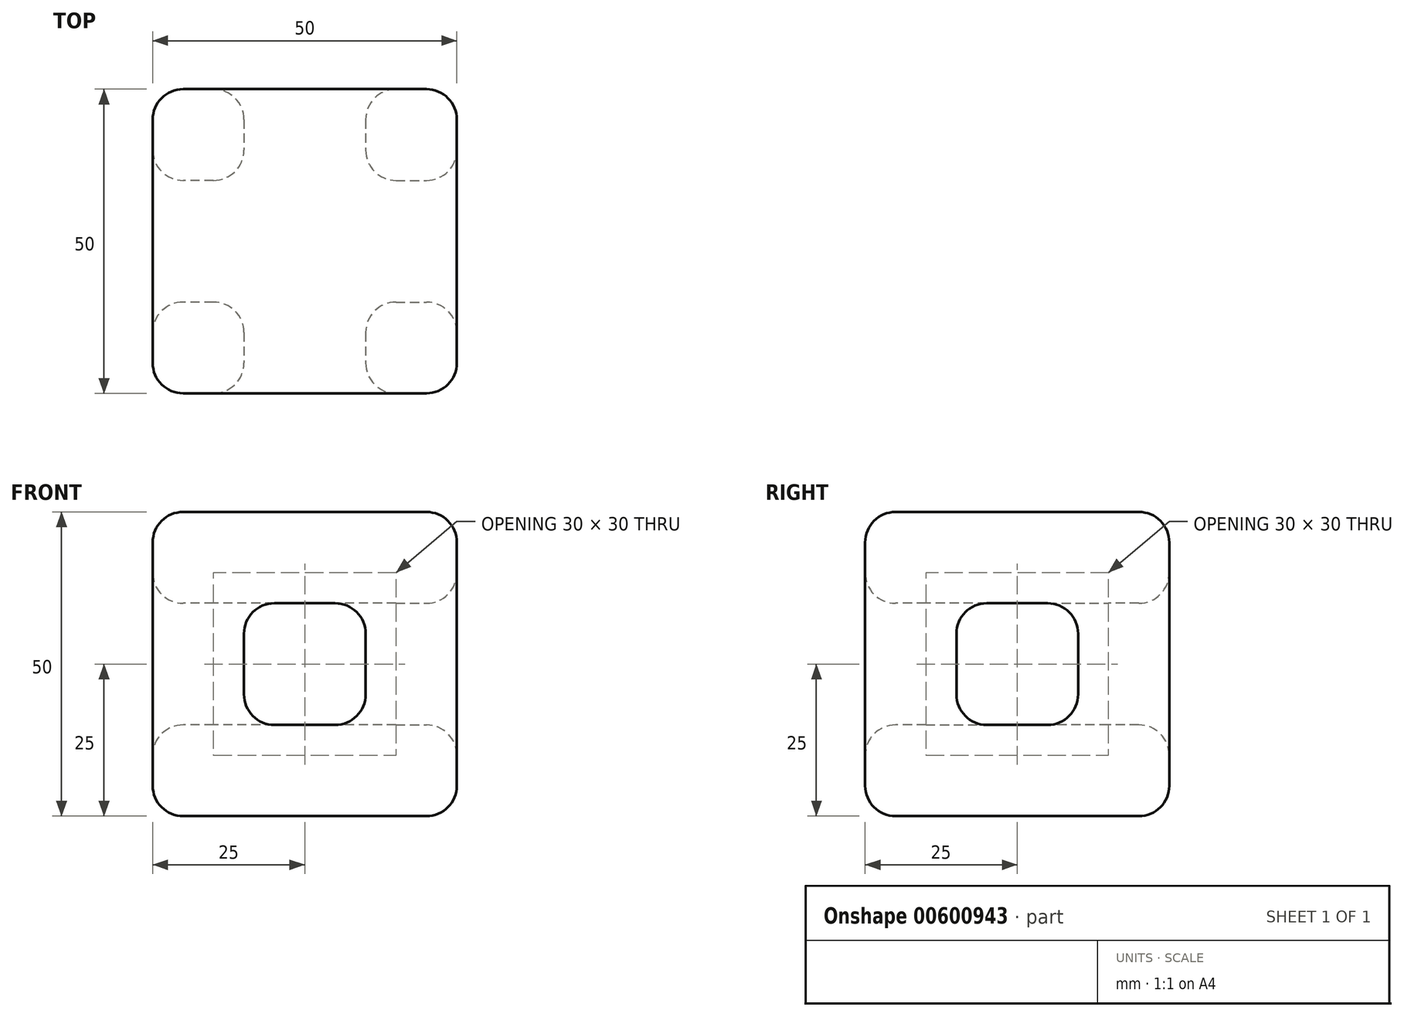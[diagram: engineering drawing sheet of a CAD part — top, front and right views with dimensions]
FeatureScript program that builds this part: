
annotation { "Feature Type Name" : "Feature", "Feature Type Description" : "" }
export const myFeature = defineFeature(function(context is Context, id is Id, definition is map)
    precondition{}
    {
        {
            var Q0;
            Q0=qCreatedBy(makeId("Front.planeOp"),FACE);
            var sketch = newSketch(context, id + "F0", { "sketchPlane" : qUnion([Q0])});
            skLineSegment(sketch, "E0.bottom", {"start": v(25, -25) * mm, "end": v(-25, -25) * mm});
            skLineSegment(sketch, "E0.top", {"start": v(25, 25) * mm, "end": v(-25, 25) * mm});
            skLineSegment(sketch, "E0.left", {"start": v(25, -25) * mm, "end": v(25, 25) * mm});
            skLineSegment(sketch, "E0.right", {"start": v(-25, -25) * mm, "end": v(-25, 25) * mm});
            skPoint(sketch, "E0.middle", {"position": v(0, 0) * mm});
            skSolve(sketch);
        }
        {
            var Q0;
            Q0 = qSketchRegion(id + "F0", true);
            extrude(context, id + "F1", {"entities" : qUnion([Q0]), "depth" : 25 * mm, "offsetDistance" : 25 * mm, "hasSecondDirection" : true, "secondDirectionOppositeDirection" : true, "secondDirectionDepth" : 25 * mm});
        }
        {
            var Q0;
            Q0=makeQuery(id+"F1.opExtrude","CAP_FACE",FACE,{"disambiguationData":[OSD([sQuery(id+"F0.wireOp",EDGE,"E0.bottom"),sQuery(id+"F0.wireOp",EDGE,"E0.top"),sQuery(id+"F0.wireOp",EDGE,"E0.left"),sQuery(id+"F0.wireOp",EDGE,"E0.right")])],"isStart":false});
            var sketch = newSketch(context, id + "F2", { "sketchPlane" : qUnion([Q0])});
            skLineSegment(sketch, "E1.bottom", {"start": v(10, 10) * mm, "end": v(-10, 10) * mm});
            skLineSegment(sketch, "E1.top", {"start": v(10, -10) * mm, "end": v(-10, -10) * mm});
            skLineSegment(sketch, "E1.left", {"start": v(10, 10) * mm, "end": v(10, -10) * mm});
            skLineSegment(sketch, "E1.right", {"start": v(-10, 10) * mm, "end": v(-10, -10) * mm});
            skPoint(sketch, "E1.middle", {"position": v(0, 0) * mm});
            skSolve(sketch);
        }
        {
            var Q0;
            Q0=makeQuery(id+"F2.imprint","IMPRINT",FACE,{"disambiguationData":[TD([[makeQuery(id+"F2.imprint","IMPRINT",EDGE,{"derivedFrom":sQuery(id+"F2.wireOp",EDGE,"E1.bottom")}),1.0]])]});
            extrude(context, id + "F3", {"entities" : qUnion([Q0]), "operationType" : NewBodyOperationType.REMOVE, "endBound" : BoundingType.UP_TO_NEXT, "oppositeDirection" : true, "depth" : 25 * mm, "offsetDistance" : 25 * mm});
        }
        {
            var Q0;
            Q0=makeQuery(id+"F1.opExtrude","SWEPT_FACE",FACE,{"disambiguationData":[OSD([sQuery(id+"F0.wireOp",EDGE,"E0.right")])]});
            var sketch = newSketch(context, id + "F4", { "sketchPlane" : qUnion([Q0])});
            skLineSegment(sketch, "E2.bottom", {"start": v(-10, 10) * mm, "end": v(10, 10) * mm});
            skLineSegment(sketch, "E2.top", {"start": v(-10, -10) * mm, "end": v(10, -10) * mm});
            skLineSegment(sketch, "E2.left", {"start": v(-10, 10) * mm, "end": v(-10, -10) * mm});
            skLineSegment(sketch, "E2.right", {"start": v(10, 10) * mm, "end": v(10, -10) * mm});
            skPoint(sketch, "E2.middle", {"position": v(0, 0) * mm});
            skSolve(sketch);
        }
        {
            var Q0;
            Q0=makeQuery(id+"F4.imprint","IMPRINT",FACE,{"disambiguationData":[TD([[makeQuery(id+"F4.imprint","IMPRINT",EDGE,{"derivedFrom":sQuery(id+"F4.wireOp",EDGE,"E2.bottom")}),-1.0]])]});
            extrude(context, id + "F5", {"entities" : qUnion([Q0]), "operationType" : NewBodyOperationType.REMOVE, "endBound" : BoundingType.UP_TO_NEXT, "oppositeDirection" : true, "depth" : 25 * mm, "offsetDistance" : 25 * mm});
        }
        {
            var Q0;
            Q0=makeQuery(id+"F1.opExtrude","SWEPT_FACE",FACE,{"disambiguationData":[OSD([sQuery(id+"F0.wireOp",EDGE,"E0.left")])]});
            var sketch = newSketch(context, id + "F6", { "sketchPlane" : qUnion([Q0])});
            skLineSegment(sketch, "E3.bottom", {"start": v(-10, 10) * mm, "end": v(10, 10) * mm});
            skLineSegment(sketch, "E3.top", {"start": v(-10, -10) * mm, "end": v(10, -10) * mm});
            skLineSegment(sketch, "E3.left", {"start": v(-10, 10) * mm, "end": v(-10, -10) * mm});
            skLineSegment(sketch, "E3.right", {"start": v(10, 10) * mm, "end": v(10, -10) * mm});
            skPoint(sketch, "E3.middle", {"position": v(0, 0) * mm});
            skSolve(sketch);
        }
        {
            var Q0;
            Q0=makeQuery(id+"F6.imprint","IMPRINT",FACE,{"disambiguationData":[TD([[makeQuery(id+"F6.imprint","IMPRINT",EDGE,{"derivedFrom":sQuery(id+"F6.wireOp",EDGE,"E3.bottom")}),-1.0]])]});
            extrude(context, id + "F7", {"entities" : qUnion([Q0]), "operationType" : NewBodyOperationType.REMOVE, "endBound" : BoundingType.UP_TO_NEXT, "oppositeDirection" : true, "depth" : 25 * mm, "offsetDistance" : 25 * mm});
        }
        {
            var Q0;
            Q0=makeQuery(id+"F1.opExtrude","SWEPT_EDGE",EDGE,{"disambiguationData":[OSD([sQuery(id+"F0.wireOp",EDGE,"E0.top"),sQuery(id+"F0.wireOp",EDGE,"E0.right")])]});
            var Q1;
            Q1=makeQuery(id+"F1.opExtrude","SWEPT_EDGE",EDGE,{"disambiguationData":[OSD([sQuery(id+"F0.wireOp",EDGE,"E0.top"),sQuery(id+"F0.wireOp",EDGE,"E0.left")])]});
            var Q2;
            Q2=makeQuery(id+"F3.boolean.opBoolean","COPY",EDGE,{"derivedFrom":makeQuery(id+"F3.opExtrude","TWEAK_EDGE",EDGE,{"derivedFrom":[makeQuery(id+"F1.opExtrude","CAP_FACE",FACE,{"disambiguationData":[OSD([sQuery(id+"F0.wireOp",EDGE,"E0.bottom"),sQuery(id+"F0.wireOp",EDGE,"E0.top"),sQuery(id+"F0.wireOp",EDGE,"E0.left"),sQuery(id+"F0.wireOp",EDGE,"E0.right")])],"isStart":true}),makeQuery(id+"F2.imprint","IMPRINT",EDGE,{"derivedFrom":sQuery(id+"F2.wireOp",EDGE,"E1.bottom")})]})});
            var Q3;
            Q3=makeQuery(id+"F1.opExtrude","SWEPT_EDGE",EDGE,{"disambiguationData":[OSD([sQuery(id+"F0.wireOp",EDGE,"E0.bottom"),sQuery(id+"F0.wireOp",EDGE,"E0.right")])]});
            var Q4;
            Q4=makeQuery(id+"F1.opExtrude","SWEPT_EDGE",EDGE,{"disambiguationData":[OSD([sQuery(id+"F0.wireOp",EDGE,"E0.bottom"),sQuery(id+"F0.wireOp",EDGE,"E0.left")])]});
            var Q5;
            Q5=makeQuery(id+"F1.opExtrude","CAP_EDGE",EDGE,{"disambiguationData":[OSD([sQuery(id+"F0.wireOp",EDGE,"E0.top")])],"isStart":false});
            var Q6;
            Q6=makeQuery(id+"F1.opExtrude","CAP_EDGE",EDGE,{"disambiguationData":[OSD([sQuery(id+"F0.wireOp",EDGE,"E0.bottom")])],"isStart":false});
            var Q7;
            Q7=makeQuery(id+"F1.opExtrude","CAP_EDGE",EDGE,{"disambiguationData":[OSD([sQuery(id+"F0.wireOp",EDGE,"E0.top")])],"isStart":true});
            var Q8;
            Q8=makeQuery(id+"F1.opExtrude","CAP_EDGE",EDGE,{"disambiguationData":[OSD([sQuery(id+"F0.wireOp",EDGE,"E0.bottom")])],"isStart":true});
            var Q9;
            Q9=makeQuery(id+"F1.opExtrude","CAP_EDGE",EDGE,{"disambiguationData":[OSD([sQuery(id+"F0.wireOp",EDGE,"E0.left")])],"isStart":true});
            var Q10;
            Q10=makeQuery(id+"F1.opExtrude","CAP_EDGE",EDGE,{"disambiguationData":[OSD([sQuery(id+"F0.wireOp",EDGE,"E0.left")])],"isStart":false});
            var Q11;
            Q11=makeQuery(id+"F1.opExtrude","CAP_EDGE",EDGE,{"disambiguationData":[OSD([sQuery(id+"F0.wireOp",EDGE,"E0.right")])],"isStart":true});
            var Q12;
            Q12=makeQuery(id+"F1.opExtrude","CAP_EDGE",EDGE,{"disambiguationData":[OSD([sQuery(id+"F0.wireOp",EDGE,"E0.right")])],"isStart":false});
            var Q13;
            Q13=makeQuery(id+"F3.boolean.opBoolean","COPY",EDGE,{"derivedFrom":makeQuery(id+"F3.opExtrude","TWEAK_EDGE",EDGE,{"derivedFrom":[makeQuery(id+"F1.opExtrude","CAP_FACE",FACE,{"disambiguationData":[OSD([sQuery(id+"F0.wireOp",EDGE,"E0.bottom"),sQuery(id+"F0.wireOp",EDGE,"E0.top"),sQuery(id+"F0.wireOp",EDGE,"E0.left"),sQuery(id+"F0.wireOp",EDGE,"E0.right")])],"isStart":true}),makeQuery(id+"F2.imprint","IMPRINT",EDGE,{"derivedFrom":sQuery(id+"F2.wireOp",EDGE,"E1.top")})]})});
            var Q14;
            Q14=makeQuery(id+"F3.boolean.opBoolean","COPY",EDGE,{"derivedFrom":makeQuery(id+"F3.opExtrude","TWEAK_EDGE",EDGE,{"derivedFrom":[makeQuery(id+"F1.opExtrude","CAP_FACE",FACE,{"disambiguationData":[OSD([sQuery(id+"F0.wireOp",EDGE,"E0.bottom"),sQuery(id+"F0.wireOp",EDGE,"E0.top"),sQuery(id+"F0.wireOp",EDGE,"E0.left"),sQuery(id+"F0.wireOp",EDGE,"E0.right")])],"isStart":true}),makeQuery(id+"F2.imprint","IMPRINT",EDGE,{"derivedFrom":sQuery(id+"F2.wireOp",EDGE,"E1.left")})]})});
            var Q15;
            Q15=makeQuery(id+"F3.boolean.opBoolean","COPY",EDGE,{"derivedFrom":makeQuery(id+"F3.opExtrude","TWEAK_EDGE",EDGE,{"derivedFrom":[makeQuery(id+"F1.opExtrude","CAP_FACE",FACE,{"disambiguationData":[OSD([sQuery(id+"F0.wireOp",EDGE,"E0.bottom"),sQuery(id+"F0.wireOp",EDGE,"E0.top"),sQuery(id+"F0.wireOp",EDGE,"E0.left"),sQuery(id+"F0.wireOp",EDGE,"E0.right")])],"isStart":true}),makeQuery(id+"F2.imprint","IMPRINT",EDGE,{"derivedFrom":sQuery(id+"F2.wireOp",EDGE,"E1.right")})]})});
            var Q16;
            Q16=makeQuery(id+"F7.boolean.opBoolean","COPY",EDGE,{"derivedFrom":makeQuery(id+"F7.opExtrude","TWEAK_EDGE",EDGE,{"derivedFrom":[makeQuery(id+"F3.boolean.opBoolean","COPY",FACE,{"derivedFrom":makeQuery(id+"F3.opExtrude","SWEPT_FACE",FACE,{"disambiguationData":[OSD([sQuery(id+"F2.wireOp",EDGE,"E1.left")])]})}),makeQuery(id+"F6.imprint","IMPRINT",EDGE,{"derivedFrom":sQuery(id+"F6.wireOp",EDGE,"E3.left")})]})});
            var Q17;
            Q17=makeQuery(id+"F1.opExtrude","CAP_FACE",FACE,{"disambiguationData":[OSD([sQuery(id+"F0.wireOp",EDGE,"E0.bottom"),sQuery(id+"F0.wireOp",EDGE,"E0.top"),sQuery(id+"F0.wireOp",EDGE,"E0.left"),sQuery(id+"F0.wireOp",EDGE,"E0.right")])],"isStart":true});
            var Q18;
            Q18=makeQuery(id+"F5.boolean.opBoolean","COPY",EDGE,{"derivedFrom":makeQuery(id+"F5.opExtrude","SWEPT_EDGE",EDGE,{"disambiguationData":[OSD([sQuery(id+"F4.wireOp",EDGE,"E2.bottom"),sQuery(id+"F4.wireOp",EDGE,"E2.left")])]})});
            var Q19;
            Q19=makeQuery(id+"F3.boolean.opBoolean","COPY",EDGE,{"derivedFrom":makeQuery(id+"F3.opExtrude","CAP_EDGE",EDGE,{"disambiguationData":[OSD([sQuery(id+"F2.wireOp",EDGE,"E1.bottom")])],"isStart":true})});
            var Q20;
            Q20=makeQuery(id+"F3.boolean.opBoolean","COPY",EDGE,{"derivedFrom":makeQuery(id+"F3.opExtrude","CAP_EDGE",EDGE,{"disambiguationData":[OSD([sQuery(id+"F2.wireOp",EDGE,"E1.top")])],"isStart":true})});
            var Q21;
            Q21=makeQuery(id+"F3.boolean.opBoolean","COPY",EDGE,{"derivedFrom":makeQuery(id+"F3.opExtrude","CAP_EDGE",EDGE,{"disambiguationData":[OSD([sQuery(id+"F2.wireOp",EDGE,"E1.right")])],"isStart":true})});
            var Q22;
            Q22=makeQuery(id+"F5.boolean.opBoolean","COPY",EDGE,{"derivedFrom":makeQuery(id+"F5.opExtrude","CAP_EDGE",EDGE,{"disambiguationData":[OSD([sQuery(id+"F4.wireOp",EDGE,"E2.left")])],"isStart":true})});
            var Q23;
            Q23=makeQuery(id+"F5.boolean.opBoolean","COPY",EDGE,{"derivedFrom":makeQuery(id+"F5.opExtrude","SWEPT_EDGE",EDGE,{"disambiguationData":[OSD([sQuery(id+"F4.wireOp",EDGE,"E2.top"),sQuery(id+"F4.wireOp",EDGE,"E2.right")])]})});
            var Q24;
            Q24=makeQuery(id+"F5.boolean.opBoolean","COPY",EDGE,{"derivedFrom":makeQuery(id+"F5.opExtrude","SWEPT_EDGE",EDGE,{"disambiguationData":[OSD([sQuery(id+"F4.wireOp",EDGE,"E2.top"),sQuery(id+"F4.wireOp",EDGE,"E2.left")])]})});
            var Q25;
            Q25=makeQuery(id+"F7.boolean.opBoolean","COPY",EDGE,{"derivedFrom":makeQuery(id+"F7.opExtrude","TWEAK_EDGE",EDGE,{"derivedFrom":[makeQuery(id+"F3.boolean.opBoolean","COPY",FACE,{"derivedFrom":makeQuery(id+"F3.opExtrude","SWEPT_FACE",FACE,{"disambiguationData":[OSD([sQuery(id+"F2.wireOp",EDGE,"E1.left")])]})}),makeQuery(id+"F6.imprint","IMPRINT",EDGE,{"derivedFrom":sQuery(id+"F6.wireOp",EDGE,"E3.right")})]})});
            var Q26;
            Q26=makeQuery(id+"F7.boolean.opBoolean","COPY",EDGE,{"derivedFrom":makeQuery(id+"F7.opExtrude","SWEPT_EDGE",EDGE,{"disambiguationData":[OSD([sQuery(id+"F6.wireOp",EDGE,"E3.bottom"),sQuery(id+"F6.wireOp",EDGE,"E3.left")])]})});
            var Q27;
            Q27=makeQuery(id+"F7.boolean.opBoolean","COPY",EDGE,{"derivedFrom":makeQuery(id+"F7.opExtrude","SWEPT_EDGE",EDGE,{"disambiguationData":[OSD([sQuery(id+"F6.wireOp",EDGE,"E3.bottom"),sQuery(id+"F6.wireOp",EDGE,"E3.right")])]})});
            var Q28;
            Q28=makeQuery(id+"F7.boolean.opBoolean","COPY",EDGE,{"derivedFrom":makeQuery(id+"F7.opExtrude","SWEPT_EDGE",EDGE,{"disambiguationData":[OSD([sQuery(id+"F6.wireOp",EDGE,"E3.top"),sQuery(id+"F6.wireOp",EDGE,"E3.left")])]})});
            var Q29;
            Q29=makeQuery(id+"F7.boolean.opBoolean","COPY",EDGE,{"derivedFrom":makeQuery(id+"F7.opExtrude","SWEPT_EDGE",EDGE,{"disambiguationData":[OSD([sQuery(id+"F6.wireOp",EDGE,"E3.top"),sQuery(id+"F6.wireOp",EDGE,"E3.right")])]})});
            var Q30;
            Q30=makeQuery(id+"F7.boolean.opBoolean","COPY",EDGE,{"derivedFrom":makeQuery(id+"F7.opExtrude","CAP_EDGE",EDGE,{"disambiguationData":[OSD([sQuery(id+"F6.wireOp",EDGE,"E3.left")])],"isStart":true})});
            var Q31;
            Q31=makeQuery(id+"F7.boolean.opBoolean","COPY",EDGE,{"derivedFrom":makeQuery(id+"F7.opExtrude","CAP_EDGE",EDGE,{"disambiguationData":[OSD([sQuery(id+"F6.wireOp",EDGE,"E3.right")])],"isStart":true})});
            var Q32;
            Q32=makeQuery(id+"F1.opExtrude","SWEPT_FACE",FACE,{"disambiguationData":[OSD([sQuery(id+"F0.wireOp",EDGE,"E0.top")])]});
            var Q33;
            Q33=makeQuery(id+"F1.opExtrude","SWEPT_FACE",FACE,{"disambiguationData":[OSD([sQuery(id+"F0.wireOp",EDGE,"E0.bottom")])]});
            var Q34;
            Q34=makeQuery(id+"F7.boolean.opBoolean","MERGE",FACE,{"derivedFrom":[makeQuery(id+"F5.boolean.opBoolean","MERGE",FACE,{"derivedFrom":[makeQuery(id+"F3.boolean.opBoolean","COPY",FACE,{"derivedFrom":makeQuery(id+"F3.opExtrude","SWEPT_FACE",FACE,{"disambiguationData":[OSD([sQuery(id+"F2.wireOp",EDGE,"E1.bottom")])]})}),makeQuery(id+"F5.opExtrude","SWEPT_FACE",FACE,{"disambiguationData":[OSD([sQuery(id+"F4.wireOp",EDGE,"E2.bottom")])]})]}),makeQuery(id+"F7.opExtrude","SWEPT_FACE",FACE,{"disambiguationData":[OSD([sQuery(id+"F6.wireOp",EDGE,"E3.bottom")])]})]});
            var Q35;
            Q35=makeQuery(id+"F5.boolean.opBoolean","COPY",EDGE,{"derivedFrom":makeQuery(id+"F5.opExtrude","TWEAK_EDGE",EDGE,{"derivedFrom":[makeQuery(id+"F3.boolean.opBoolean","COPY",FACE,{"derivedFrom":makeQuery(id+"F3.opExtrude","SWEPT_FACE",FACE,{"disambiguationData":[OSD([sQuery(id+"F2.wireOp",EDGE,"E1.right")])]})}),makeQuery(id+"F4.imprint","IMPRINT",EDGE,{"derivedFrom":sQuery(id+"F4.wireOp",EDGE,"E2.left")})]})});
            var Q36;
            Q36=makeQuery(id+"F1.opExtrude","CAP_FACE",FACE,{"disambiguationData":[OSD([sQuery(id+"F0.wireOp",EDGE,"E0.bottom"),sQuery(id+"F0.wireOp",EDGE,"E0.top"),sQuery(id+"F0.wireOp",EDGE,"E0.left"),sQuery(id+"F0.wireOp",EDGE,"E0.right")])],"isStart":false});
            var Q37;
            Q37=makeQuery(id+"F3.boolean.opBoolean","COPY",EDGE,{"derivedFrom":makeQuery(id+"F3.opExtrude","CAP_EDGE",EDGE,{"disambiguationData":[OSD([sQuery(id+"F2.wireOp",EDGE,"E1.left")])],"isStart":true})});
            var Q38;
            {var subQ0=sQuery(id+"F2.wireOp",EDGE,"E1.right");var subQ1=sQuery(id+"F2.wireOp",EDGE,"E1.top");Q38=makeQuery(id+"F5.boolean.opBoolean","SPLIT",EDGE,{"disambiguationData":[TD([makeQuery(id+"F5.opExtrude","SWEPT_FACE",FACE,{"disambiguationData":[OSD([sQuery(id+"F4.wireOp",EDGE,"E2.left")])]})])],"derivedFrom":makeQuery(id+"F3.boolean.opBoolean","COPY",EDGE,{"derivedFrom":makeQuery(id+"F3.opExtrude","SWEPT_EDGE",EDGE,{"disambiguationData":[OSD([subQ1,subQ0])]})})});}
            var Q39;
            {var subQ0=sQuery(id+"F2.wireOp",EDGE,"E1.right");var subQ1=sQuery(id+"F2.wireOp",EDGE,"E1.bottom");Q39=makeQuery(id+"F5.boolean.opBoolean","SPLIT",EDGE,{"disambiguationData":[TD([makeQuery(id+"F5.opExtrude","SWEPT_FACE",FACE,{"disambiguationData":[OSD([sQuery(id+"F4.wireOp",EDGE,"E2.left")])]})])],"derivedFrom":makeQuery(id+"F3.boolean.opBoolean","COPY",EDGE,{"derivedFrom":makeQuery(id+"F3.opExtrude","SWEPT_EDGE",EDGE,{"disambiguationData":[OSD([subQ1,subQ0])]})})});}
            var Q40;
            Q40=makeQuery(id+"F5.boolean.opBoolean","COPY",EDGE,{"derivedFrom":makeQuery(id+"F5.opExtrude","CAP_EDGE",EDGE,{"disambiguationData":[OSD([sQuery(id+"F4.wireOp",EDGE,"E2.right")])],"isStart":true})});
            var Q41;
            Q41=makeQuery(id+"F5.boolean.opBoolean","COPY",EDGE,{"derivedFrom":makeQuery(id+"F5.opExtrude","CAP_EDGE",EDGE,{"disambiguationData":[OSD([sQuery(id+"F4.wireOp",EDGE,"E2.top")])],"isStart":true})});
            var Q42;
            Q42=makeQuery(id+"F5.boolean.opBoolean","COPY",EDGE,{"derivedFrom":makeQuery(id+"F5.opExtrude","CAP_EDGE",EDGE,{"disambiguationData":[OSD([sQuery(id+"F4.wireOp",EDGE,"E2.bottom")])],"isStart":true})});
            var Q43;
            Q43=makeQuery(id+"F1.opExtrude","SWEPT_FACE",FACE,{"disambiguationData":[OSD([sQuery(id+"F0.wireOp",EDGE,"E0.right")])]});
            var Q44;
            Q44=makeQuery(id+"F5.boolean.opBoolean","COPY",EDGE,{"derivedFrom":makeQuery(id+"F5.opExtrude","SWEPT_EDGE",EDGE,{"disambiguationData":[OSD([sQuery(id+"F4.wireOp",EDGE,"E2.bottom"),sQuery(id+"F4.wireOp",EDGE,"E2.right")])]})});
            var Q45;
            Q45=makeQuery(id+"F5.boolean.opBoolean","COPY",FACE,{"derivedFrom":makeQuery(id+"F5.opExtrude","SWEPT_FACE",FACE,{"disambiguationData":[OSD([sQuery(id+"F4.wireOp",EDGE,"E2.left")])]})});
            var Q46;
            Q46=makeQuery(id+"F7.boolean.opBoolean","MERGE",FACE,{"derivedFrom":[makeQuery(id+"F5.boolean.opBoolean","MERGE",FACE,{"derivedFrom":[makeQuery(id+"F3.boolean.opBoolean","COPY",FACE,{"derivedFrom":makeQuery(id+"F3.opExtrude","SWEPT_FACE",FACE,{"disambiguationData":[OSD([sQuery(id+"F2.wireOp",EDGE,"E1.top")])]})}),makeQuery(id+"F5.opExtrude","SWEPT_FACE",FACE,{"disambiguationData":[OSD([sQuery(id+"F4.wireOp",EDGE,"E2.top")])]})]}),makeQuery(id+"F7.opExtrude","SWEPT_FACE",FACE,{"disambiguationData":[OSD([sQuery(id+"F6.wireOp",EDGE,"E3.top")])]})]});
            var Q47;
            Q47=makeQuery(id+"F7.boolean.opBoolean","COPY",FACE,{"derivedFrom":makeQuery(id+"F7.opExtrude","SWEPT_FACE",FACE,{"disambiguationData":[OSD([sQuery(id+"F6.wireOp",EDGE,"E3.left")])]})});
            var Q48;
            Q48=makeQuery(id+"F7.boolean.opBoolean","COPY",FACE,{"derivedFrom":makeQuery(id+"F7.opExtrude","SWEPT_FACE",FACE,{"disambiguationData":[OSD([sQuery(id+"F6.wireOp",EDGE,"E3.right")])]})});
            var Q49;
            Q49=makeQuery(id+"F1.opExtrude","SWEPT_FACE",FACE,{"disambiguationData":[OSD([sQuery(id+"F0.wireOp",EDGE,"E0.left")])]});
            var Q50;
            Q50=makeQuery(id+"F7.boolean.opBoolean","SPLIT",FACE,{"disambiguationData":[TD([makeQuery(id+"F7.opExtrude","SWEPT_FACE",FACE,{"disambiguationData":[OSD([sQuery(id+"F6.wireOp",EDGE,"E3.right")])]})])],"derivedFrom":makeQuery(id+"F3.boolean.opBoolean","COPY",FACE,{"derivedFrom":makeQuery(id+"F3.opExtrude","SWEPT_FACE",FACE,{"disambiguationData":[OSD([sQuery(id+"F2.wireOp",EDGE,"E1.left")])]})})});
            var Q51;
            Q51=makeQuery(id+"F7.boolean.opBoolean","COPY",EDGE,{"derivedFrom":makeQuery(id+"F7.opExtrude","CAP_EDGE",EDGE,{"disambiguationData":[OSD([sQuery(id+"F6.wireOp",EDGE,"E3.bottom")])],"isStart":true})});
            var Q52;
            Q52=makeQuery(id+"F7.boolean.opBoolean","COPY",EDGE,{"derivedFrom":makeQuery(id+"F7.opExtrude","CAP_EDGE",EDGE,{"disambiguationData":[OSD([sQuery(id+"F6.wireOp",EDGE,"E3.top")])],"isStart":true})});
            var Q53;
            {var subQ0=sQuery(id+"F2.wireOp",EDGE,"E1.left");var subQ1=sQuery(id+"F2.wireOp",EDGE,"E1.bottom");Q53=makeQuery(id+"F7.boolean.opBoolean","SPLIT",EDGE,{"disambiguationData":[TD([makeQuery(id+"F7.opExtrude","SWEPT_FACE",FACE,{"disambiguationData":[OSD([sQuery(id+"F6.wireOp",EDGE,"E3.right")])]})])],"derivedFrom":makeQuery(id+"F3.boolean.opBoolean","COPY",EDGE,{"derivedFrom":makeQuery(id+"F3.opExtrude","SWEPT_EDGE",EDGE,{"disambiguationData":[OSD([subQ1,subQ0])]})})});}
            var Q54;
            {var subQ0=sQuery(id+"F2.wireOp",EDGE,"E1.left");var subQ1=sQuery(id+"F2.wireOp",EDGE,"E1.bottom");Q54=makeQuery(id+"F7.boolean.opBoolean","SPLIT",EDGE,{"disambiguationData":[TD([makeQuery(id+"F7.opExtrude","SWEPT_FACE",FACE,{"disambiguationData":[OSD([sQuery(id+"F6.wireOp",EDGE,"E3.left")])]})])],"derivedFrom":makeQuery(id+"F3.boolean.opBoolean","COPY",EDGE,{"derivedFrom":makeQuery(id+"F3.opExtrude","SWEPT_EDGE",EDGE,{"disambiguationData":[OSD([subQ1,subQ0])]})})});}
            var Q55;
            {var subQ0=sQuery(id+"F2.wireOp",EDGE,"E1.top");var subQ1=sQuery(id+"F2.wireOp",EDGE,"E1.left");Q55=makeQuery(id+"F7.boolean.opBoolean","SPLIT",EDGE,{"disambiguationData":[TD([makeQuery(id+"F7.opExtrude","SWEPT_FACE",FACE,{"disambiguationData":[OSD([sQuery(id+"F6.wireOp",EDGE,"E3.right")])]})])],"derivedFrom":makeQuery(id+"F3.boolean.opBoolean","COPY",EDGE,{"derivedFrom":makeQuery(id+"F3.opExtrude","SWEPT_EDGE",EDGE,{"disambiguationData":[OSD([subQ0,subQ1])]})})});}
            var Q56;
            {var subQ0=sQuery(id+"F2.wireOp",EDGE,"E1.left");var subQ1=sQuery(id+"F2.wireOp",EDGE,"E1.top");Q56=makeQuery(id+"F7.boolean.opBoolean","SPLIT",EDGE,{"disambiguationData":[TD([makeQuery(id+"F7.opExtrude","SWEPT_FACE",FACE,{"disambiguationData":[OSD([sQuery(id+"F6.wireOp",EDGE,"E3.left")])]})])],"derivedFrom":makeQuery(id+"F3.boolean.opBoolean","COPY",EDGE,{"derivedFrom":makeQuery(id+"F3.opExtrude","SWEPT_EDGE",EDGE,{"disambiguationData":[OSD([subQ1,subQ0])]})})});}
            var Q57;
            Q57=makeQuery(id+"F5.boolean.opBoolean","SPLIT",FACE,{"disambiguationData":[TD([makeQuery(id+"F5.opExtrude","SWEPT_FACE",FACE,{"disambiguationData":[OSD([sQuery(id+"F4.wireOp",EDGE,"E2.left")])]})])],"derivedFrom":makeQuery(id+"F3.boolean.opBoolean","COPY",FACE,{"derivedFrom":makeQuery(id+"F3.opExtrude","SWEPT_FACE",FACE,{"disambiguationData":[OSD([sQuery(id+"F2.wireOp",EDGE,"E1.right")])]})})});
            var Q58;
            Q58=makeQuery(id+"F5.boolean.opBoolean","COPY",FACE,{"derivedFrom":makeQuery(id+"F5.opExtrude","SWEPT_FACE",FACE,{"disambiguationData":[OSD([sQuery(id+"F4.wireOp",EDGE,"E2.right")])]})});
            var Q59;
            Q59=makeQuery(id+"F5.boolean.opBoolean","COPY",EDGE,{"derivedFrom":makeQuery(id+"F5.opExtrude","TWEAK_EDGE",EDGE,{"derivedFrom":[makeQuery(id+"F3.boolean.opBoolean","COPY",FACE,{"derivedFrom":makeQuery(id+"F3.opExtrude","SWEPT_FACE",FACE,{"disambiguationData":[OSD([sQuery(id+"F2.wireOp",EDGE,"E1.right")])]})}),makeQuery(id+"F4.imprint","IMPRINT",EDGE,{"derivedFrom":sQuery(id+"F4.wireOp",EDGE,"E2.right")})]})});
            var Q60;
            {var subQ0=sQuery(id+"F2.wireOp",EDGE,"E1.top");var subQ1=sQuery(id+"F2.wireOp",EDGE,"E1.right");Q60=makeQuery(id+"F5.boolean.opBoolean","SPLIT",EDGE,{"disambiguationData":[TD([makeQuery(id+"F5.opExtrude","SWEPT_FACE",FACE,{"disambiguationData":[OSD([sQuery(id+"F4.wireOp",EDGE,"E2.right")])]})])],"derivedFrom":makeQuery(id+"F3.boolean.opBoolean","COPY",EDGE,{"derivedFrom":makeQuery(id+"F3.opExtrude","SWEPT_EDGE",EDGE,{"disambiguationData":[OSD([subQ0,subQ1])]})})});}
            var Q61;
            Q61=makeQuery(id+"F7.boolean.opBoolean","SPLIT",FACE,{"disambiguationData":[TD([makeQuery(id+"F7.opExtrude","SWEPT_FACE",FACE,{"disambiguationData":[OSD([sQuery(id+"F6.wireOp",EDGE,"E3.left")])]})])],"derivedFrom":makeQuery(id+"F3.boolean.opBoolean","COPY",FACE,{"derivedFrom":makeQuery(id+"F3.opExtrude","SWEPT_FACE",FACE,{"disambiguationData":[OSD([sQuery(id+"F2.wireOp",EDGE,"E1.left")])]})})});
            var Q62;
            {var subQ0=sQuery(id+"F2.wireOp",EDGE,"E1.bottom");var subQ1=sQuery(id+"F2.wireOp",EDGE,"E1.right");Q62=makeQuery(id+"F5.boolean.opBoolean","SPLIT",EDGE,{"disambiguationData":[TD([makeQuery(id+"F5.opExtrude","SWEPT_FACE",FACE,{"disambiguationData":[OSD([sQuery(id+"F4.wireOp",EDGE,"E2.right")])]})])],"derivedFrom":makeQuery(id+"F3.boolean.opBoolean","COPY",EDGE,{"derivedFrom":makeQuery(id+"F3.opExtrude","SWEPT_EDGE",EDGE,{"disambiguationData":[OSD([subQ0,subQ1])]})})});}
            var Q63;
            Q63=makeQuery(id+"F5.boolean.opBoolean","SPLIT",FACE,{"disambiguationData":[TD([makeQuery(id+"F5.opExtrude","SWEPT_FACE",FACE,{"disambiguationData":[OSD([sQuery(id+"F4.wireOp",EDGE,"E2.right")])]})])],"derivedFrom":makeQuery(id+"F3.boolean.opBoolean","COPY",FACE,{"derivedFrom":makeQuery(id+"F3.opExtrude","SWEPT_FACE",FACE,{"disambiguationData":[OSD([sQuery(id+"F2.wireOp",EDGE,"E1.right")])]})})});
            fillet(context, id + "F8", {"entities" : qUnion([Q0, Q1, Q2, Q3, Q4, Q5, Q6, Q7, Q8, Q9, Q10, Q11, Q12, Q13, Q14, Q15, Q16, Q17, Q18, Q19, Q20, Q21, Q22, Q23, Q24, Q25, Q26, Q27, Q28, Q29, Q30, Q31, Q32, Q33, Q34, Q35, Q36, Q37, Q38, Q39, Q40, Q41, Q42, Q43, Q44, Q45, Q46, Q47, Q48, Q49, Q50, Q51, Q52, Q53, Q54, Q55, Q56, Q57, Q58, Q59, Q60, Q61, Q62, Q63]), "radius" : 5 * mm, "tangentPropagation" : true, "allowEdgeOverflow" : false});
        }
    });
